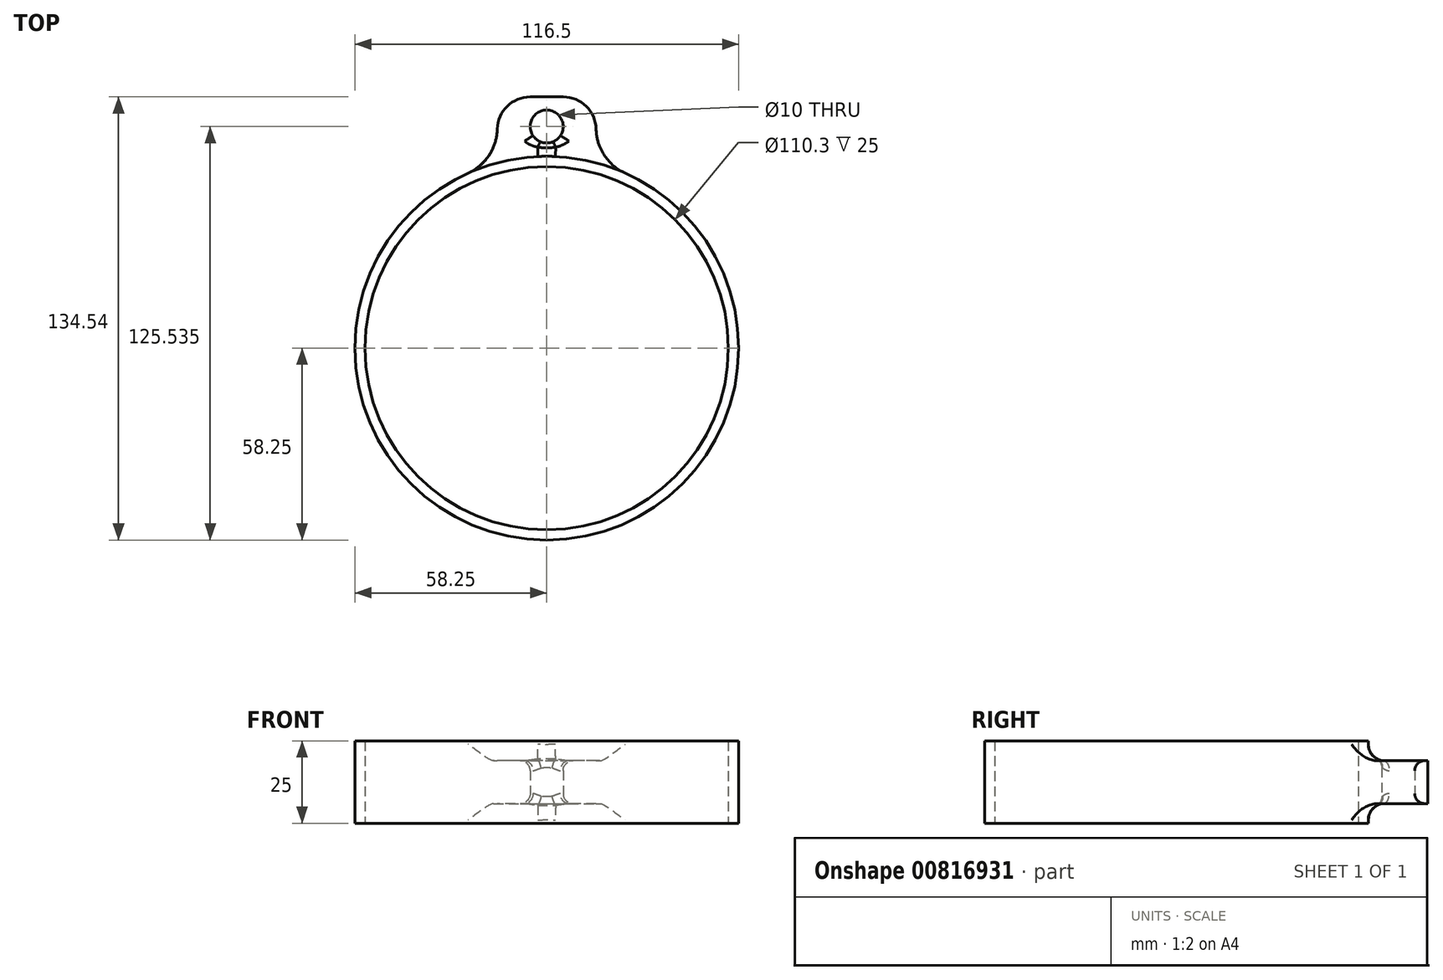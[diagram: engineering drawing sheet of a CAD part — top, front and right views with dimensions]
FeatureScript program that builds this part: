
annotation { "Feature Type Name" : "Feature", "Feature Type Description" : "" }
export const myFeature = defineFeature(function(context is Context, id is Id, definition is map)
    precondition{}
    {
        {
            var Q0;
            Q0=qCreatedBy(makeId("Top.planeOp"),FACE);
            var sketch = newSketch(context, id + "F0", { "sketchPlane" : qUnion([Q0])});
            skArc(sketch, "E0", {"start": v(-15, 56.29) * mm, "mid": v(0, -58.25) * mm, "end": v(15, 56.29) * mm});
            skCircle(sketch, "E1", {"center": v(0, 0) * mm, "radius": 55.15 * mm});
            skLineSegment(sketch, "E2", {"start": v(-15, 56.29) * mm, "end": v(-15, 76.29) * mm});
            skLineSegment(sketch, "E3", {"start": v(-15, 76.29) * mm, "end": v(15, 76.29) * mm});
            skLineSegment(sketch, "E4", {"start": v(15, 76.29) * mm, "end": v(15, 56.29) * mm});
            skLineSegment(sketch, "E5", {"start": v(0, 0) * mm, "end": v(0, 75.37) * mm, "construction": true});
            skCircle(sketch, "E6", {"center": v(0, 67.29) * mm, "radius": 5 * mm});
            skSolve(sketch);
        }
        {
            var Q0;
            Q0=makeQuery(id+"F0.imprint","IMPRINT",FACE,{"disambiguationData":[TD([[makeQuery(id+"F0.imprint","IMPRINT",EDGE,{"derivedFrom":sQuery(id+"F0.wireOp",EDGE,"E0")}),1.0]])]});
            extrude(context, id + "F1", {"entities" : qUnion([Q0]), "depth" : 25 * mm, "offsetDistance" : 25 * mm});
        }
        {
            var Q0;
            Q0=makeQuery(id+"F1.opExtrude","SWEPT_EDGE",EDGE,{"disambiguationData":[OSD([sQuery(id+"F0.wireOp",EDGE,"E0"),sQuery(id+"F0.wireOp",EDGE,"E2")])]});
            var Q1;
            Q1=makeQuery(id+"F1.opExtrude","SWEPT_EDGE",EDGE,{"disambiguationData":[OSD([sQuery(id+"F0.wireOp",EDGE,"E0"),sQuery(id+"F0.wireOp",EDGE,"E4")])]});
            fillet(context, id + "F2", {"entities" : qUnion([Q0, Q1]), "radius" : 15 * mm, "tangentPropagation" : true, "allowEdgeOverflow" : false});
        }
        {
            var Q0;
            Q0=makeQuery(id+"F1.opExtrude","SWEPT_EDGE",EDGE,{"disambiguationData":[OSD([sQuery(id+"F0.wireOp",EDGE,"E3"),sQuery(id+"F0.wireOp",EDGE,"E4")])]});
            var Q1;
            Q1=makeQuery(id+"F1.opExtrude","SWEPT_EDGE",EDGE,{"disambiguationData":[OSD([sQuery(id+"F0.wireOp",EDGE,"E2"),sQuery(id+"F0.wireOp",EDGE,"E3")])]});
            fillet(context, id + "F3", {"entities" : qUnion([Q0, Q1]), "radius" : 10 * mm, "tangentPropagation" : true, "allowEdgeOverflow" : false});
        }
        {
            var Q0;
            Q0=makeQuery(id+"F1.opExtrude","CAP_FACE",FACE,{"disambiguationData":[OSD([sQuery(id+"F0.wireOp",EDGE,"E0"),sQuery(id+"F0.wireOp",EDGE,"E1"),sQuery(id+"F0.wireOp",EDGE,"E2"),sQuery(id+"F0.wireOp",EDGE,"E3"),sQuery(id+"F0.wireOp",EDGE,"E4"),sQuery(id+"F0.wireOp",EDGE,"E6")])],"isStart":false});
            var sketch = newSketch(context, id + "F4", { "sketchPlane" : qUnion([Q0])});
            skArc(sketch, "E7.0", {"start": v(-15, 66.5) * mm, "mid": v(-17.5, 58.54) * mm, "end": v(-23.86, 53.14) * mm});
            skArc(sketch, "E7.1", {"start": v(-5, 76.29) * mm, "mid": v(-12, 73.43) * mm, "end": v(-15, 66.5) * mm});
            skLineSegment(sketch, "E7.2", {"start": v(-5, 76.29) * mm, "end": v(5, 76.29) * mm});
            skArc(sketch, "E7.3", {"start": v(15, 66.5) * mm, "mid": v(12, 73.43) * mm, "end": v(5, 76.29) * mm});
            skArc(sketch, "E7.4", {"start": v(23.86, 53.14) * mm, "mid": v(17.5, 58.54) * mm, "end": v(15, 66.5) * mm});
            skArc(sketch, "E8", {"start": v(-23.86, 53.14) * mm, "mid": v(0, 58.25) * mm, "end": v(23.86, 53.14) * mm});
            skSolve(sketch);
        }
        {
            var Q0;
            Q0=makeQuery(id+"F4.imprint","IMPRINT",FACE,{"disambiguationData":[TD([[makeQuery(id+"F4.imprint","IMPRINT",EDGE,{"derivedFrom":sQuery(id+"F4.wireOp",EDGE,"E7.0")}),1.0]])]});
            extrude(context, id + "F5", {"entities" : qUnion([Q0]), "operationType" : NewBodyOperationType.REMOVE, "oppositeDirection" : true, "depth" : (6) * mm, "offsetDistance" : 25 * mm});
        }
        {
            var Q0;
            Q0=makeQuery(id+"F1.opExtrude","CAP_FACE",FACE,{"disambiguationData":[OSD([sQuery(id+"F0.wireOp",EDGE,"E0"),sQuery(id+"F0.wireOp",EDGE,"E1"),sQuery(id+"F0.wireOp",EDGE,"E2"),sQuery(id+"F0.wireOp",EDGE,"E3"),sQuery(id+"F0.wireOp",EDGE,"E4"),sQuery(id+"F0.wireOp",EDGE,"E6")])],"isStart":true});
            var sketch = newSketch(context, id + "F6", { "sketchPlane" : qUnion([Q0])});
            skArc(sketch, "E9.0", {"start": v(15, -66.5) * mm, "mid": v(17.5, -58.54) * mm, "end": v(23.86, -53.14) * mm});
            skArc(sketch, "E9.1", {"start": v(5, -76.29) * mm, "mid": v(12, -73.43) * mm, "end": v(15, -66.5) * mm});
            skLineSegment(sketch, "E9.2", {"start": v(-5, -76.29) * mm, "end": v(5, -76.29) * mm});
            skArc(sketch, "E9.3", {"start": v(-15, -66.5) * mm, "mid": v(-12, -73.43) * mm, "end": v(-5, -76.29) * mm});
            skArc(sketch, "E9.4", {"start": v(-23.86, -53.14) * mm, "mid": v(-17.5, -58.54) * mm, "end": v(-15, -66.5) * mm});
            skArc(sketch, "E10", {"start": v(23.86, -53.14) * mm, "mid": v(0, -58.25) * mm, "end": v(-23.86, -53.14) * mm});
            skSolve(sketch);
        }
        {
            var Q0;
            Q0=makeQuery(id+"F6.imprint","IMPRINT",FACE,{"disambiguationData":[TD([[makeQuery(id+"F6.imprint","IMPRINT",EDGE,{"derivedFrom":sQuery(id+"F6.wireOp",EDGE,"E9.0")}),1.0]])]});
            extrude(context, id + "F7", {"entities" : qUnion([Q0]), "operationType" : NewBodyOperationType.REMOVE, "oppositeDirection" : true, "depth" : (6) * mm, "offsetDistance" : 25 * mm});
        }
        {
            var Q0;
            Q0=makeQuery(id+"F5.boolean.opBoolean","COPY",EDGE,{"derivedFrom":makeQuery(id+"F5.opExtrude","CAP_EDGE",EDGE,{"disambiguationData":[OSD([sQuery(id+"F4.wireOp",EDGE,"E8")])],"isStart":false})});
            var Q1;
            Q1=makeQuery(id+"F7.boolean.opBoolean","COPY",EDGE,{"derivedFrom":makeQuery(id+"F7.opExtrude","CAP_EDGE",EDGE,{"disambiguationData":[OSD([sQuery(id+"F6.wireOp",EDGE,"E10")])],"isStart":false})});
            fillet(context, id + "F8", {"entities" : qUnion([Q0, Q1]), "radius" : 5 * mm, "tangentPropagation" : true, "allowEdgeOverflow" : false});
        }
        {
            var Q0;
            Q0=makeQuery(id+"F8.opFillet","BLEND_EDGE",EDGE,{"blendedFrom":[makeQuery(id+"F5.boolean.opBoolean","COPY",EDGE,{"derivedFrom":makeQuery(id+"F5.opExtrude","CAP_EDGE",EDGE,{"disambiguationData":[OSD([sQuery(id+"F4.wireOp",EDGE,"E8")])],"isStart":false})}),makeQuery(id+"F1.opExtrude","SWEPT_FACE",FACE,{"disambiguationData":[OSD([sQuery(id+"F0.wireOp",EDGE,"E6")])]})],"blendedInto":[makeQuery(id+"F1.opExtrude","SWEPT_FACE",FACE,{"disambiguationData":[OSD([sQuery(id+"F0.wireOp",EDGE,"E6")])]})]});
            var Q1;
            Q1=makeQuery(id+"F8.opFillet","BLEND_EDGE",EDGE,{"blendedFrom":[makeQuery(id+"F7.boolean.opBoolean","COPY",EDGE,{"derivedFrom":makeQuery(id+"F7.opExtrude","CAP_EDGE",EDGE,{"disambiguationData":[OSD([sQuery(id+"F6.wireOp",EDGE,"E10")])],"isStart":false})}),makeQuery(id+"F1.opExtrude","SWEPT_FACE",FACE,{"disambiguationData":[OSD([sQuery(id+"F0.wireOp",EDGE,"E6")])]})],"blendedInto":[makeQuery(id+"F1.opExtrude","SWEPT_FACE",FACE,{"disambiguationData":[OSD([sQuery(id+"F0.wireOp",EDGE,"E6")])]})]});
            fillet(context, id + "F9", {"entities" : qUnion([Q0, Q1]), "radius" : (3) * mm, "tangentPropagation" : true, "allowEdgeOverflow" : false});
        }
    });
